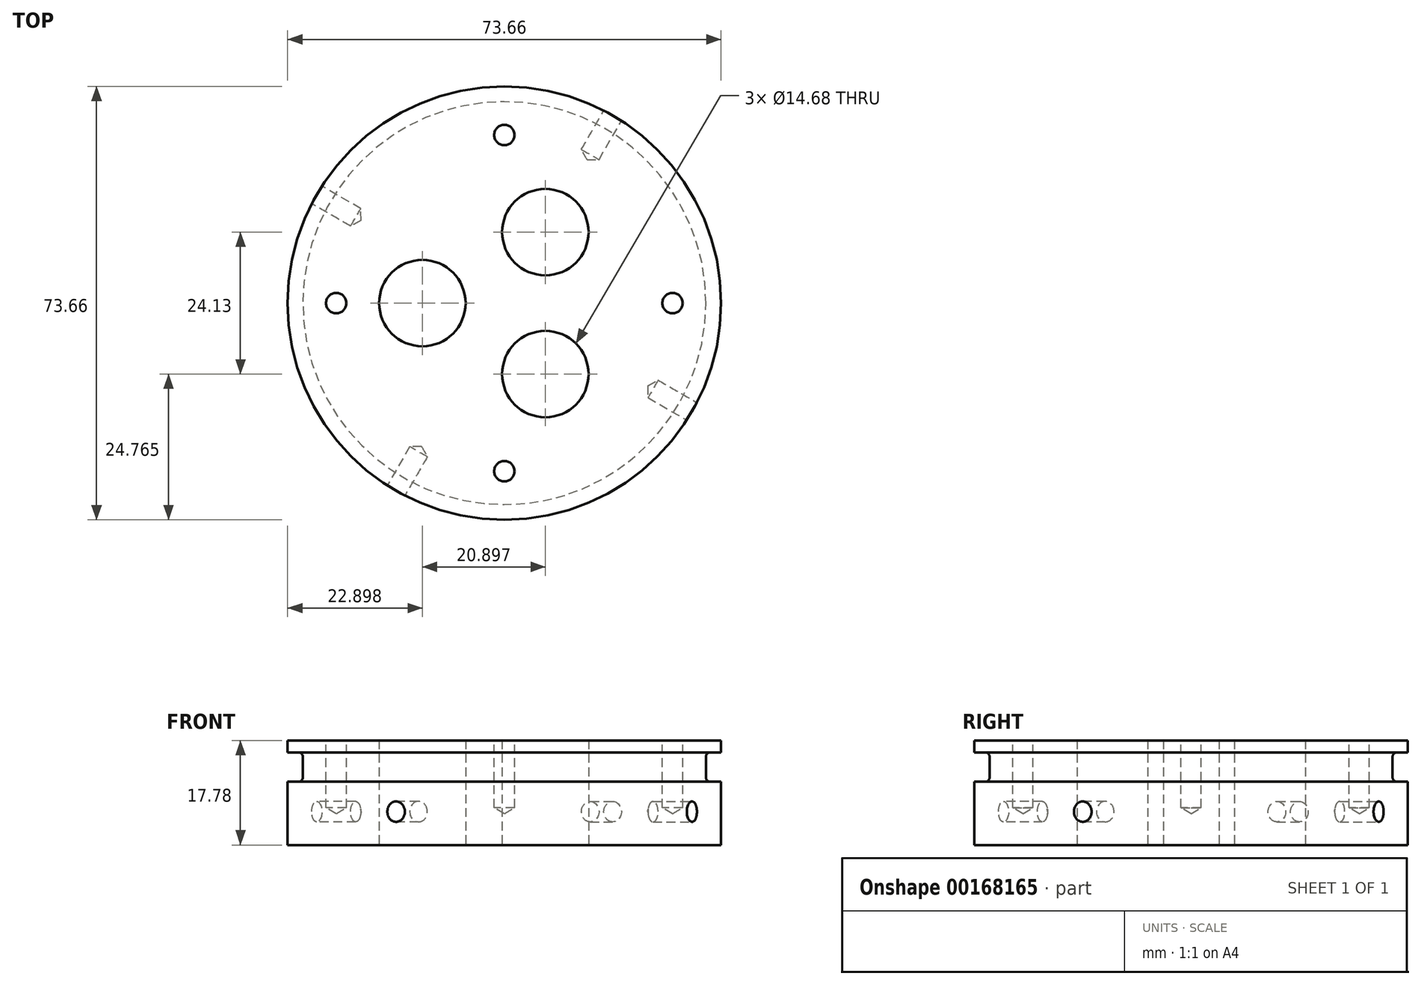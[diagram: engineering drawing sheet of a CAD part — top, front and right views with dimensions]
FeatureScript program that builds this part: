
annotation { "Feature Type Name" : "Feature", "Feature Type Description" : "" }
export const myFeature = defineFeature(function(context is Context, id is Id, definition is map)
    precondition{}
    {
        {
            var Q0;
            Q0=qCreatedBy(makeId("Top.planeOp"),FACE);
            var sketch = newSketch(context, id + "F0", { "sketchPlane" : qUnion([Q0])});
            skCircle(sketch, "E0", {"center": v(0, 0) * mm, "radius": 36.83 * mm});
            skSolve(sketch);
        }
        {
            var Q0;
            Q0=makeQuery(id+"F0.imprint","IMPRINT",FACE,{"disambiguationData":[TD([[makeQuery(id+"F0.imprint","IMPRINT",EDGE,{"derivedFrom":sQuery(id+"F0.wireOp",EDGE,"E0")}),1.0]])]});
            extrude(context, id + "F1", {"entities" : qUnion([Q0]), "depth" : 17.78 * mm});
        }
        {
            var Q0;
            {var subQ0=makeQuery(id+"FhJubWmbG7UBd7M_1.boolean.opBoolean","COPY",FACE,{"derivedFrom":makeQuery(id+"FhJubWmbG7UBd7M_1.opExtrude","SWEPT_FACE",FACE,{"disambiguationData":[OSD([sQuery(id+"FRuIeaWD6VeLny9_1.wireOp",EDGE,"idePJaX5-tPPE-BKw2-N1m4-zZUQrY6AHjir")])]})});Q0=makeQuery(id+"FOQC5dfjhO448EJ_1.boolean.opBoolean","SPLIT",FACE,{"disambiguationData":[TD([subQ0])],"derivedFrom":makeQuery(id+"FkcieFRIapZdHPD_1.boolean.opBoolean","SPLIT",FACE,{"disambiguationData":[TD([subQ0])],"derivedFrom":makeQuery(id+"F1.opExtrude","CAP_FACE",FACE,{"disambiguationData":[OSD([sQuery(id+"F0.wireOp",EDGE,"E0")])],"isStart":false})})});}
            var sketch = newSketch(context, id + "F2", { "sketchPlane" : qUnion([Q0])});
            skCircle(sketch, "E1", {"center": v(0, 0) * mm, "radius": 28.58 * mm, "construction": true});
            skLineSegment(sketch, "E2", {"start": v(0, 0) * mm, "end": v(28.57, 0) * mm, "construction": true});
            skPoint(sketch, "E3", {"position": v(28.58, 0) * mm});
            skPoint(sketch, "E4.1.0", {"position": v(0, 28.58) * mm});
            skPoint(sketch, "E4.2.0", {"position": v(-28.58, 0) * mm});
            skPoint(sketch, "E4.3.0", {"position": v(0, -28.58) * mm});
            skSolve(sketch);
        }
        {
            var Q0;
            Q0=sQuery(id+"F2.wireOp",VERTEX,"E3");
            var Q1;
            Q1=sQuery(id+"F2.wireOp",VERTEX,"E4.3.0");
            var Q2;
            Q2=sQuery(id+"F2.wireOp",VERTEX,"E4.2.0");
            var Q3;
            Q3=sQuery(id+"F2.wireOp",VERTEX,"E4.1.0");
            var Q4;
            Q4=makeQuery(id+"F1.opExtrude","SWEPT_BODY",BODY,{"disambiguationData":[OSD([sQuery(id+"F0.wireOp",EDGE,"E0")])]});
            hole(context, id + "F3", {"style" : HoleStyle.SIMPLE, "endStyle" : HoleEndStyle.BLIND, "standardTappedOrClearance" : lookupTablePath({ "standard" : "ANSI", "engagement" : "75%", "pitch" : "32 tpi", "size" : "#8", "type" : "Tapped" }), "standardBlindInLast" : lookupTablePath({ "standard" : "ANSI", "engagement" : "75%", "pitch" : "32 tpi", "size" : "#8", "type" : "Tapped" }), "holeDiameter" : 3.45 * mm, "holeDepth" : 11.43 * mm, "locations" : qUnion([Q0, Q1, Q2, Q3]), "scope" : qUnion([Q4]), "majorDiameter" : 4.17 * mm});
        }
        {
            var Q0;
            Q0=makeQuery(id+"FOQC5dfjhO448EJ_1.boolean.opBoolean","SPLIT",FACE,{"disambiguationData":[TD([makeQuery(id+"FhJubWmbG7UBd7M_1.boolean.opBoolean","COPY",FACE,{"derivedFrom":makeQuery(id+"FhJubWmbG7UBd7M_1.opExtrude","SWEPT_FACE",FACE,{"disambiguationData":[OSD([sQuery(id+"FRuIeaWD6VeLny9_1.wireOp",EDGE,"idePJaX5-tPPE-BKw2-N1m4-zZUQrY6AHjir")])]})})])],"derivedFrom":makeQuery(id+"F1.opExtrude","CAP_FACE",FACE,{"disambiguationData":[OSD([sQuery(id+"F0.wireOp",EDGE,"E0")])],"isStart":false})});
            cPlane(context, id + "F4", {"entities" : qUnion([Q0]), "cplaneType" : CPlaneType.OFFSET, "offset" : 2.03 * mm, "oppositeDirection" : true, "width" : 152.4 * mm, "height" : 152.4 * mm});
        }
        {
            var Q0;
            Q0=qCreatedBy(id+"F4.planeOp",FACE);
            var sketch = newSketch(context, id + "F5", { "sketchPlane" : qUnion([Q0])});
            skCircle(sketch, "E5", {"center": v(0, 0) * mm, "radius": 34.24 * mm});
            skCircle(sketch, "E6.0", {"center": v(0, 0) * mm, "radius": 36.83 * mm});
            skSolve(sketch);
        }
        {
            var Q0;
            Q0=qSketchRegion(id+"F5",true);
            extrude(context, id + "F6", {"entities" : qUnion([Q0]), "operationType" : NewBodyOperationType.REMOVE, "oppositeDirection" : true, "depth" : 5 * mm});
        }
        {
            var Q0;
            Q0=makeQuery(id+"F6.boolean.opBoolean","COPY",EDGE,{"derivedFrom":makeQuery(id+"F6.opExtrude","CAP_EDGE",EDGE,{"disambiguationData":[OSD([sQuery(id+"F5.wireOp",EDGE,"E5")])],"isStart":false})});
            var Q1;
            Q1=makeQuery(id+"F6.boolean.opBoolean","COPY",EDGE,{"derivedFrom":makeQuery(id+"F6.opExtrude","CAP_EDGE",EDGE,{"disambiguationData":[OSD([sQuery(id+"F5.wireOp",EDGE,"E5")])],"isStart":true})});
            fillet(context, id + "F7", {"entities" : qUnion([Q0, Q1]), "radius" : 0.76 * mm, "tangentPropagation" : true, "allowEdgeOverflow" : false});
        }
        {
            var Q0;
            {var subQ1=sQuery(id+"F0.wireOp",EDGE,"E0");var subQ2=makeQuery(id+"F1.opExtrude","SWEPT_FACE",FACE,{"disambiguationData":[OSD([subQ1])]});Q0=makeQuery(id+"FkcieFRIapZdHPD_1.boolean.opBoolean","SPLIT",FACE,{"disambiguationData":[TD([subQ2])],"derivedFrom":makeQuery(id+"F1.opExtrude","CAP_FACE",FACE,{"disambiguationData":[OSD([subQ1])],"isStart":false})});}
            var sketch = newSketch(context, id + "F8", { "sketchPlane" : qUnion([Q0])});
            skCircle(sketch, "E7.0", {"center": v(0, 0) * mm, "radius": 36.83 * mm, "construction": true});
            skPoint(sketch, "E8", {"position": v(-18.41, -31.9) * mm});
            skLineSegment(sketch, "E9", {"start": v(0, -36.83) * mm, "end": v(0, 0) * mm, "construction": true});
            skLineSegment(sketch, "E10", {"start": v(0, 0) * mm, "end": v(-17.96, -31.1) * mm, "construction": true});
            skLineSegment(sketch, "E11", {"start": v(-17.96, -31.1) * mm, "end": v(-18.41, -31.9) * mm, "construction": true});
            skLineSegment(sketch, "E12", {"start": v(0, 0) * mm, "end": v(18.41, 31.9) * mm, "construction": true});
            skLineSegment(sketch, "E13", {"start": v(18.41, 31.9) * mm, "end": v(0, 0) * mm, "construction": true});
            skLineSegment(sketch, "E14", {"start": v(31.9, -18.41) * mm, "end": v(0, 0) * mm, "construction": true});
            skLineSegment(sketch, "E15", {"start": v(0, 0) * mm, "end": v(-31.9, 18.41) * mm, "construction": true});
            skPoint(sketch, "E16", {"position": v(18.41, 31.9) * mm});
            skPoint(sketch, "E17", {"position": v(31.9, -18.41) * mm});
            skPoint(sketch, "E18", {"position": v(-31.9, 18.41) * mm});
            skSolve(sketch);
        }
        {
            var Q0;
            Q0=qCreatedBy(makeId("Front.planeOp"),FACE);
            var sketch = newSketch(context, id + "F9", { "sketchPlane" : qUnion([Q0])});
            skLineSegment(sketch, "E19", {"start": v(0, 0) * mm, "end": v(0, 38.57) * mm, "construction": true});
            skSolve(sketch);
        }
        {
            var Q0;
            Q0=sQuery(id+"F9.wireOp",EDGE,"E19");
            cPlane(context, id + "F10", {"entities" : qUnion([Q0]), "cplaneType" : CPlaneType.LINE_ANGLE, "offset" : 25.4 * mm, "angle" : 60 * degree, "width" : 152.4 * mm, "height" : 152.4 * mm});
        }
        {
            var Q0;
            Q0=sQuery(id+"F8.wireOp",VERTEX,"E8");
            var Q1;
            Q1=qCreatedBy(id+"F10.planeOp",FACE);
            cPlane(context, id + "F11", {"entities" : qUnion([Q0, Q1]), "cplaneType" : CPlaneType.PLANE_POINT, "offset" : 25.4 * mm, "width" : 152.4 * mm, "height" : 152.4 * mm});
        }
        {
            var Q0;
            Q0=qCreatedBy(id+"F11.planeOp",FACE);
            var Q1;
            Q1=sQuery(id+"F8.wireOp",VERTEX,"E16");
            cPlane(context, id + "F12", {"entities" : qUnion([Q0, Q1]), "cplaneType" : CPlaneType.PLANE_POINT, "offset" : 25.4 * mm, "width" : 152.4 * mm, "height" : 152.4 * mm});
        }
        {
            var Q0;
            Q0=sQuery(id+"F9.wireOp",EDGE,"E19");
            cPlane(context, id + "F13", {"entities" : qUnion([Q0]), "cplaneType" : CPlaneType.LINE_ANGLE, "offset" : 25.4 * mm, "angle" : 150 * degree, "width" : 152.4 * mm, "height" : 152.4 * mm});
        }
        {
            var Q0;
            Q0=sQuery(id+"F8.wireOp",VERTEX,"E18");
            var Q1;
            Q1=qCreatedBy(id+"F13.planeOp",FACE);
            cPlane(context, id + "F14", {"entities" : qUnion([Q0, Q1]), "cplaneType" : CPlaneType.PLANE_POINT, "offset" : 25.4 * mm, "width" : 152.4 * mm, "height" : 152.4 * mm});
        }
        {
            var Q0;
            Q0=qCreatedBy(id+"F13.planeOp",FACE);
            var Q1;
            Q1=sQuery(id+"F8.wireOp",VERTEX,"E17");
            cPlane(context, id + "F15", {"entities" : qUnion([Q0, Q1]), "cplaneType" : CPlaneType.PLANE_POINT, "offset" : 25.4 * mm, "width" : 152.4 * mm, "height" : 152.4 * mm});
        }
        {
            var Q0;
            Q0=qCreatedBy(id+"F11.planeOp",FACE);
            var sketch = newSketch(context, id + "F16", { "sketchPlane" : qUnion([Q0])});
            skLineSegment(sketch, "E20", {"start": v(0, 0) * mm, "end": v(0, 5.66) * mm, "construction": true});
            skPoint(sketch, "E21", {"position": v(0, 5.66) * mm});
            skSolve(sketch);
        }
        {
            var Q0;
            Q0=qCreatedBy(id+"F12.planeOp",FACE);
            var sketch = newSketch(context, id + "F17", { "sketchPlane" : qUnion([Q0])});
            skPoint(sketch, "E22", {"position": v(0, 5.66) * mm});
            skLineSegment(sketch, "E23.0", {"start": v(0, 0) * mm, "end": v(0, 5.66) * mm, "construction": true});
            skSolve(sketch);
        }
        {
            var Q0;
            Q0=qCreatedBy(id+"F14.planeOp",FACE);
            var sketch = newSketch(context, id + "F18", { "sketchPlane" : qUnion([Q0])});
            skLineSegment(sketch, "E24", {"start": v(0, 0) * mm, "end": v(0, 5.66) * mm, "construction": true});
            skLineSegment(sketch, "E25.0", {"start": v(-36.83, 0) * mm, "end": v(-36.83, 5.66) * mm, "construction": true});
            skPoint(sketch, "E26", {"position": v(0, 5.66) * mm});
            skLineSegment(sketch, "E27", {"start": v(-36.83, 5.66) * mm, "end": v(0, 5.66) * mm, "construction": true});
            skSolve(sketch);
        }
        {
            var Q0;
            Q0=qCreatedBy(id+"F15.planeOp",FACE);
            var sketch = newSketch(context, id + "F19", { "sketchPlane" : qUnion([Q0])});
            skLineSegment(sketch, "E28.0", {"start": v(0, 0) * mm, "end": v(0, 5.66) * mm, "construction": true});
            skPoint(sketch, "E29", {"position": v(0, 5.66) * mm});
            skSolve(sketch);
        }
        {
            var Q0;
            Q0=sQuery(id+"F19.wireOp",VERTEX,"E29");
            var Q1;
            Q1=makeQuery(id+"F1.opExtrude","SWEPT_BODY",BODY,{"disambiguationData":[OSD([sQuery(id+"F0.wireOp",EDGE,"E0")])]});
            hole(context, id + "F20", {"style" : HoleStyle.SIMPLE, "endStyle" : HoleEndStyle.BLIND, "oppositeDirection" : true, "standardTappedOrClearance" : lookupTablePath({ "standard" : "ANSI", "engagement" : "75%", "pitch" : "32 tpi", "size" : "#8", "type" : "Tapped" }), "standardBlindInLast" : lookupTablePath({ "standard" : "ANSI", "engagement" : "75%", "pitch" : "32 tpi", "size" : "#8", "type" : "Tapped" }), "holeDiameter" : 3.45 * mm, "holeDepth" : 7.62 * mm, "locations" : qUnion([Q0]), "scope" : qUnion([Q1]), "majorDiameter" : 4.17 * mm});
        }
        {
            var Q0;
            Q0=sQuery(id+"F18.wireOp",VERTEX,"E26");
            var Q1;
            Q1=makeQuery(id+"F1.opExtrude","SWEPT_BODY",BODY,{"disambiguationData":[OSD([sQuery(id+"F0.wireOp",EDGE,"E0")])]});
            hole(context, id + "F21", {"style" : HoleStyle.SIMPLE, "endStyle" : HoleEndStyle.BLIND, "standardTappedOrClearance" : lookupTablePath({ "standard" : "ANSI", "engagement" : "75%", "pitch" : "32 tpi", "size" : "#8", "type" : "Tapped" }), "standardBlindInLast" : lookupTablePath({ "standard" : "ANSI", "engagement" : "75%", "pitch" : "32 tpi", "size" : "#8", "type" : "Tapped" }), "holeDiameter" : 3.45 * mm, "holeDepth" : 7.62 * mm, "locations" : qUnion([Q0]), "scope" : qUnion([Q1]), "majorDiameter" : 4.17 * mm});
        }
        {
            var Q0;
            Q0=sQuery(id+"F16.wireOp",VERTEX,"E21");
            var Q1;
            Q1=makeQuery(id+"F1.opExtrude","SWEPT_BODY",BODY,{"disambiguationData":[OSD([sQuery(id+"F0.wireOp",EDGE,"E0")])]});
            hole(context, id + "F22", {"style" : HoleStyle.SIMPLE, "endStyle" : HoleEndStyle.BLIND, "oppositeDirection" : true, "standardTappedOrClearance" : lookupTablePath({ "standard" : "ANSI", "engagement" : "75%", "pitch" : "32 tpi", "size" : "#8", "type" : "Tapped" }), "standardBlindInLast" : lookupTablePath({ "standard" : "ANSI", "engagement" : "75%", "pitch" : "32 tpi", "size" : "#8", "type" : "Tapped" }), "holeDiameter" : 3.45 * mm, "holeDepth" : 7.62 * mm, "locations" : qUnion([Q0]), "scope" : qUnion([Q1]), "majorDiameter" : 4.17 * mm});
        }
        {
            var Q0;
            Q0=sQuery(id+"F17.wireOp",VERTEX,"E22");
            var Q1;
            Q1=makeQuery(id+"F1.opExtrude","SWEPT_BODY",BODY,{"disambiguationData":[OSD([sQuery(id+"F0.wireOp",EDGE,"E0")])]});
            hole(context, id + "F23", {"style" : HoleStyle.SIMPLE, "endStyle" : HoleEndStyle.BLIND, "standardTappedOrClearance" : lookupTablePath({ "standard" : "ANSI", "engagement" : "75%", "pitch" : "32 tpi", "size" : "#8", "type" : "Tapped" }), "standardBlindInLast" : lookupTablePath({ "standard" : "ANSI", "engagement" : "75%", "pitch" : "32 tpi", "size" : "#8", "type" : "Tapped" }), "holeDiameter" : 3.45 * mm, "holeDepth" : 7.62 * mm, "locations" : qUnion([Q0]), "scope" : qUnion([Q1]), "majorDiameter" : 4.17 * mm});
        }
        {
            var Q0;
            Q0=makeQuery(id+"F1.opExtrude","CAP_FACE",FACE,{"disambiguationData":[OSD([sQuery(id+"F0.wireOp",EDGE,"E0")])],"isStart":true});
            var sketch = newSketch(context, id + "F24", { "sketchPlane" : qUnion([Q0])});
            skPoint(sketch, "E30", {"position": v(-13.93, 0) * mm});
            skPoint(sketch, "E31.1.0", {"position": v(6.97, -12.07) * mm});
            skPoint(sketch, "E31.2.0", {"position": v(6.97, 12.07) * mm});
            skPoint(sketch, "E31.center", {"position": v(0, 0) * mm});
            skSolve(sketch);
        }
        {
            var Q0;
            Q0=sQuery(id+"F24.wireOp",VERTEX,"4a09c47b-9143-4afa-8474-e2cbf5050e91");
            var Q1;
            Q1=sQuery(id+"F24.wireOp",VERTEX,"E31.1.0");
            var Q2;
            Q2=sQuery(id+"F24.wireOp",VERTEX,"E30");
            var Q3;
            Q3=sQuery(id+"F24.wireOp",VERTEX,"E31.2.0");
            var Q4;
            Q4=makeQuery(id+"F1.opExtrude","SWEPT_BODY",BODY,{"disambiguationData":[OSD([sQuery(id+"F0.wireOp",EDGE,"E0")])]});
            hole(context, id + "F25", {"style" : HoleStyle.SIMPLE, "endStyle" : HoleEndStyle.THROUGH, "holeDiameter" : 14.68 * mm, "locations" : qUnion([Q0, Q1, Q2, Q3]), "scope" : qUnion([Q4]), "isTappedThrough" : true});
        }
    });
